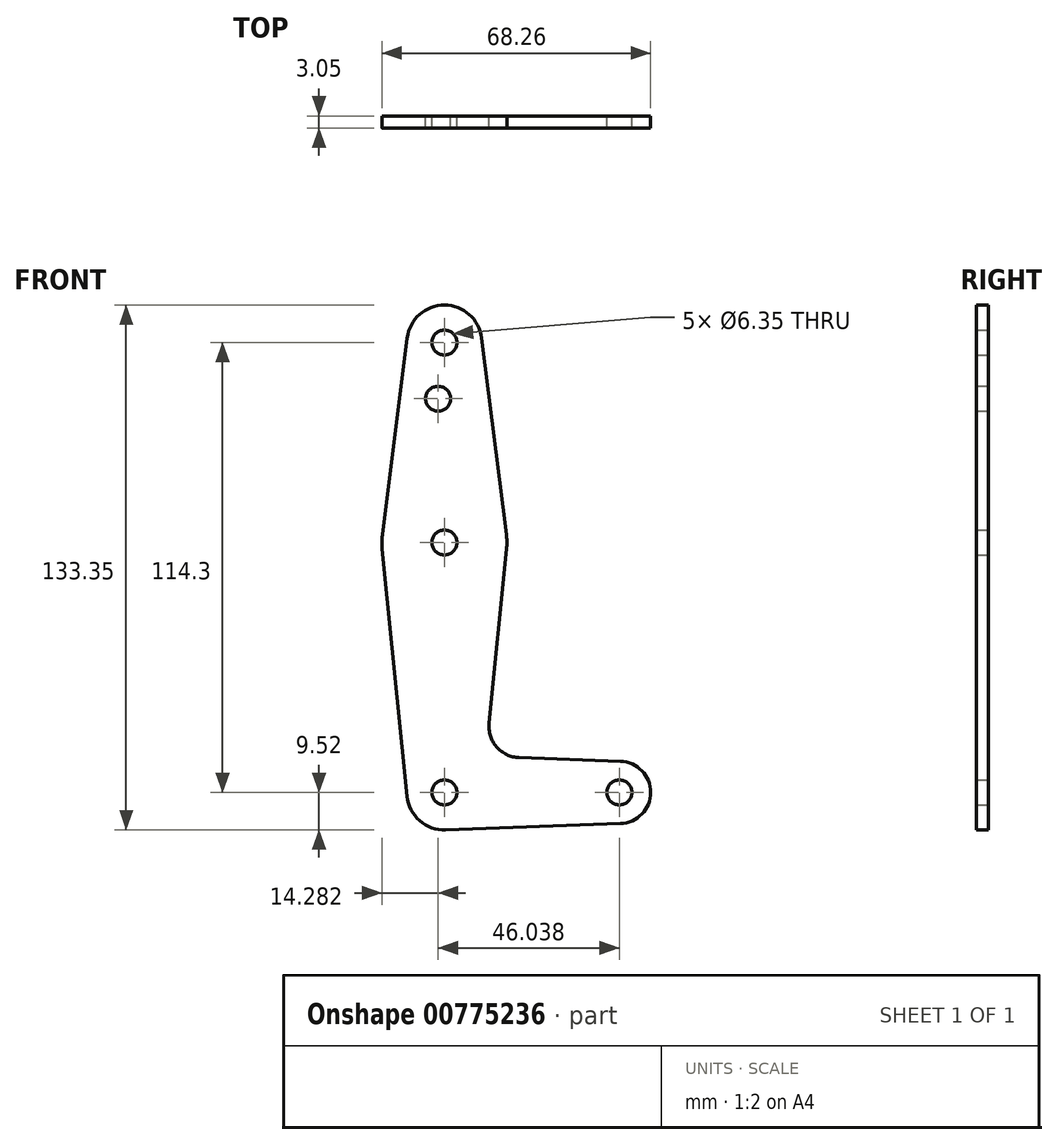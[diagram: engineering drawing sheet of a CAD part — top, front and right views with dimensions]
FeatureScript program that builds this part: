
annotation { "Feature Type Name" : "Feature", "Feature Type Description" : "" }
export const myFeature = defineFeature(function(context is Context, id is Id, definition is map)
    precondition{}
    {
        {
            var Q0;
            Q0=qCreatedBy(makeId("Front.planeOp"),FACE);
            var sketch = newSketch(context, id + "F0", { "sketchPlane" : qUnion([Q0])});
            skCircle(sketch, "E0", {"center": v(0, 0) * mm, "radius": 9.53 * mm});
            skLineSegment(sketch, "E1", {"start": v(0, 0) * mm, "end": v(0, 114.3) * mm, "construction": true});
            skLineSegment(sketch, "E2", {"start": v(0, 0) * mm, "end": v(44.45, 0) * mm, "construction": true});
            skCircle(sketch, "E3", {"center": v(44.45, 0) * mm, "radius": 7.94 * mm});
            skCircle(sketch, "E4", {"center": v(0, 114.3) * mm, "radius": 9.53 * mm});
            skCircle(sketch, "E5", {"center": v(0, 63.5) * mm, "radius": 15.88 * mm});
            skLineSegment(sketch, "E6", {"start": v(-15.75, 65.48) * mm, "end": v(-9.45, 115.5) * mm});
            skLineSegment(sketch, "E7", {"start": v(9.45, 115.5) * mm, "end": v(15.75, 65.48) * mm});
            skLineSegment(sketch, "E8", {"start": v(-15.8, 61.91) * mm, "end": v(-9.48, -0.95) * mm});
            skLineSegment(sketch, "E9", {"start": v(15.8, 61.91) * mm, "end": v(11.34, 17.6) * mm});
            skLineSegment(sketch, "E10", {"start": v(18.97, 8.85) * mm, "end": v(44.73, 7.93) * mm});
            skLineSegment(sketch, "E11", {"start": v(0.34, -9.52) * mm, "end": v(44.73, -7.93) * mm});
            skCircle(sketch, "E12", {"center": v(0, 114.3) * mm, "radius": 3.18 * mm});
            skCircle(sketch, "E13", {"center": v(0, 63.5) * mm, "radius": 3.18 * mm});
            skCircle(sketch, "E14", {"center": v(0, 0) * mm, "radius": 3.18 * mm});
            skCircle(sketch, "E15", {"center": v(44.45, 0) * mm, "radius": 3.18 * mm});
            skCircle(sketch, "E16", {"center": v(-1.59, 100.03) * mm, "radius": 3.18 * mm});
            skArc(sketch, "E17.filletArc", {"start": v(11.34, 17.6) * mm, "mid": v(13.26, 11.57) * mm, "end": v(18.97, 8.85) * mm});
            skSolve(sketch);
        }
        {
            var Q0;
            Q0 = qSketchRegion(id + "F0", true);
            extrude(context, id + "F1", {"entities" : qUnion([Q0]), "depth" : 3.05 * mm, "offsetDistance" : 25.4 * mm});
        }
    });
